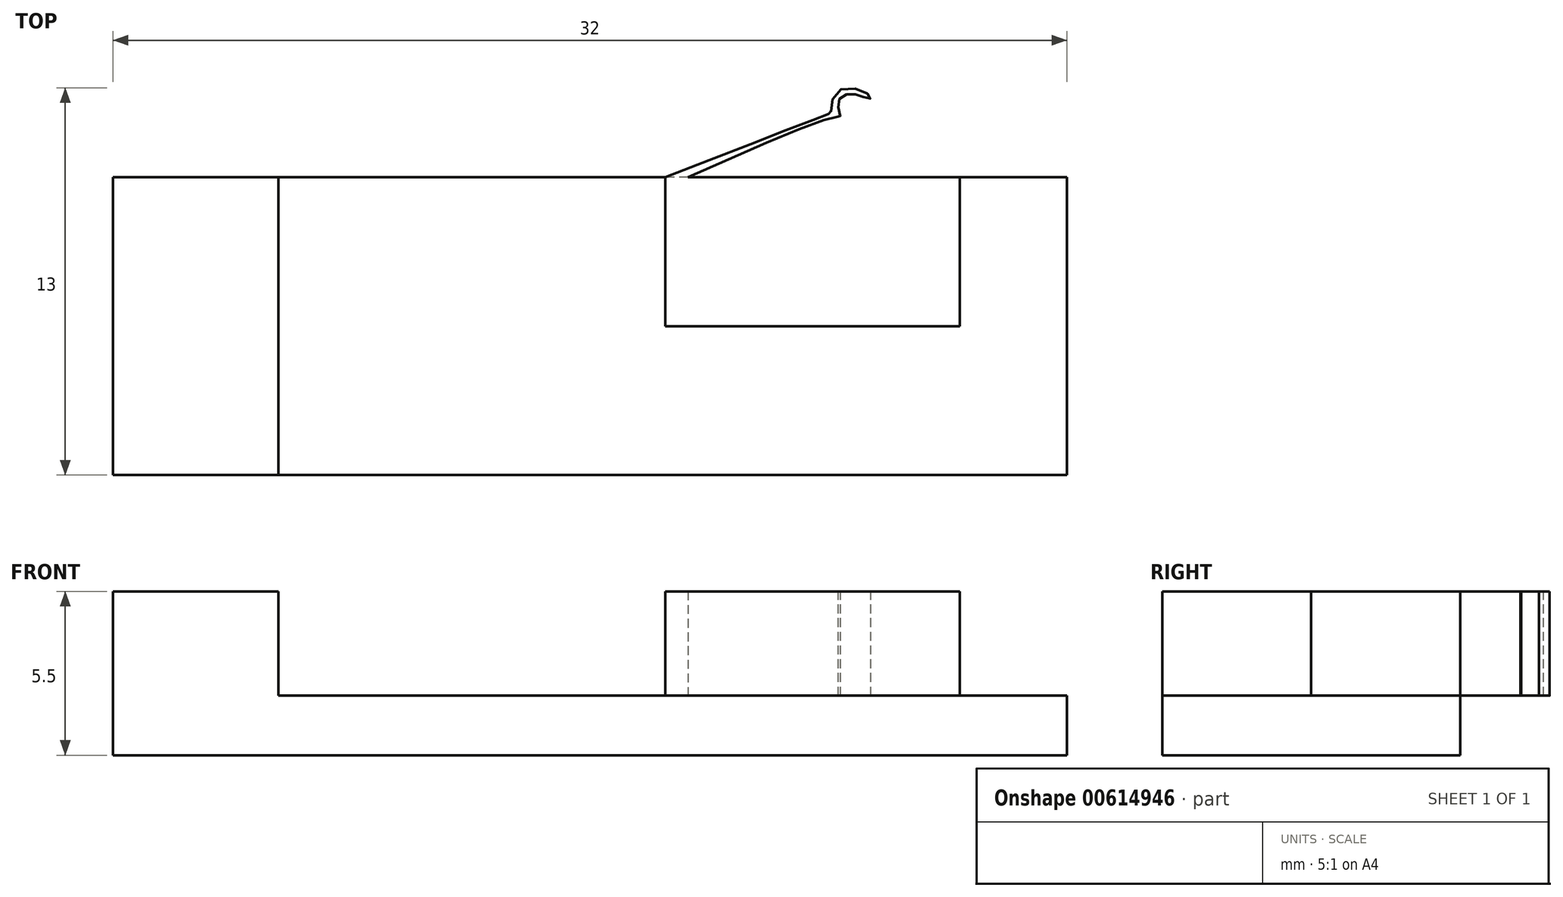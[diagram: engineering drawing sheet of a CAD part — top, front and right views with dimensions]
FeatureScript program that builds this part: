
annotation { "Feature Type Name" : "Feature", "Feature Type Description" : "" }
export const myFeature = defineFeature(function(context is Context, id is Id, definition is map)
    precondition{}
    {
        {
            var Q0;
            Q0=qCreatedBy(makeId("Top.planeOp"),FACE);
            var sketch = newSketch(context, id + "F0", { "sketchPlane" : qUnion([Q0])});
            skLineSegment(sketch, "E0.bottom", {"start": v(16, 5) * mm, "end": v(-16, 5) * mm});
            skLineSegment(sketch, "E0.top", {"start": v(16, -5) * mm, "end": v(-16, -5) * mm});
            skLineSegment(sketch, "E0.left", {"start": v(16, 5) * mm, "end": v(16, -5) * mm});
            skLineSegment(sketch, "E0.right", {"start": v(-16, 5) * mm, "end": v(-16, -5) * mm});
            skPoint(sketch, "E0.middle", {"position": v(0, 0) * mm});
            skSolve(sketch);
        }
        {
            var Q0;
            Q0 = qSketchRegion(id + "F0", true);
            extrude(context, id + "F1", {"entities" : qUnion([Q0]), "depth" : 2 * mm, "offsetDistance" : 25 * mm});
        }
        {
            var Q0;
            Q0=makeQuery(id+"F1.opExtrude","CAP_FACE",FACE,{"disambiguationData":[OSD([sQuery(id+"F0.wireOp",EDGE,"E0.bottom"),sQuery(id+"F0.wireOp",EDGE,"E0.top"),sQuery(id+"F0.wireOp",EDGE,"E0.left"),sQuery(id+"F0.wireOp",EDGE,"E0.right")])],"isStart":false});
            var sketch = newSketch(context, id + "F2", { "sketchPlane" : qUnion([Q0])});
            skLineSegment(sketch, "E1.bottom", {"start": v(-16, 5) * mm, "end": v(-10.45, 5) * mm});
            skLineSegment(sketch, "E1.top", {"start": v(-16, -5) * mm, "end": v(-10.45, -5) * mm});
            skLineSegment(sketch, "E1.left", {"start": v(-16, 5) * mm, "end": v(-16, -5) * mm});
            skLineSegment(sketch, "E1.right", {"start": v(-10.45, 5) * mm, "end": v(-10.45, -5) * mm});
            skPoint(sketch, "E1.middle", {"position": v(-13.23, 0) * mm});
            skLineSegment(sketch, "E2.bottom", {"start": v(2.53, 0) * mm, "end": v(12.4, 0) * mm});
            skLineSegment(sketch, "E2.top", {"start": v(2.53, 5) * mm, "end": v(12.4, 5) * mm});
            skLineSegment(sketch, "E2.left", {"start": v(2.53, 0) * mm, "end": v(2.53, 5) * mm});
            skLineSegment(sketch, "E2.right", {"start": v(12.4, 0) * mm, "end": v(12.4, 5) * mm});
            skFitSpline(sketch, "E3", {"points": [v(2.53, 5) * mm, v(8.07, 7.15) * mm, v(8.1, 7.17) * mm, v(8.26, 7.84) * mm, v(9.23, 7.86) * mm, v(9.41, 7.65) * mm, v(9.16, 7.7) * mm, v(8.8, 7.8) * mm, v(8.4, 7.68) * mm, v(8.34, 7.3) * mm, v(8.4, 7.02) * mm, v(8.36, 7.03) * mm, v(3.3, 5) * mm], "startDerivative": vector(34.28, 13.36) * mm, "endDerivative": vector(-31.64, -14.02) * mm});
            skSolve(sketch);
        }
        {
            var Q0;
            Q0 = qSketchRegion(id + "F2", true);
            extrude(context, id + "F3", {"entities" : qUnion([Q0]), "operationType" : NewBodyOperationType.ADD, "depth" : 3.5 * mm, "offsetDistance" : 25 * mm});
        }
    });
